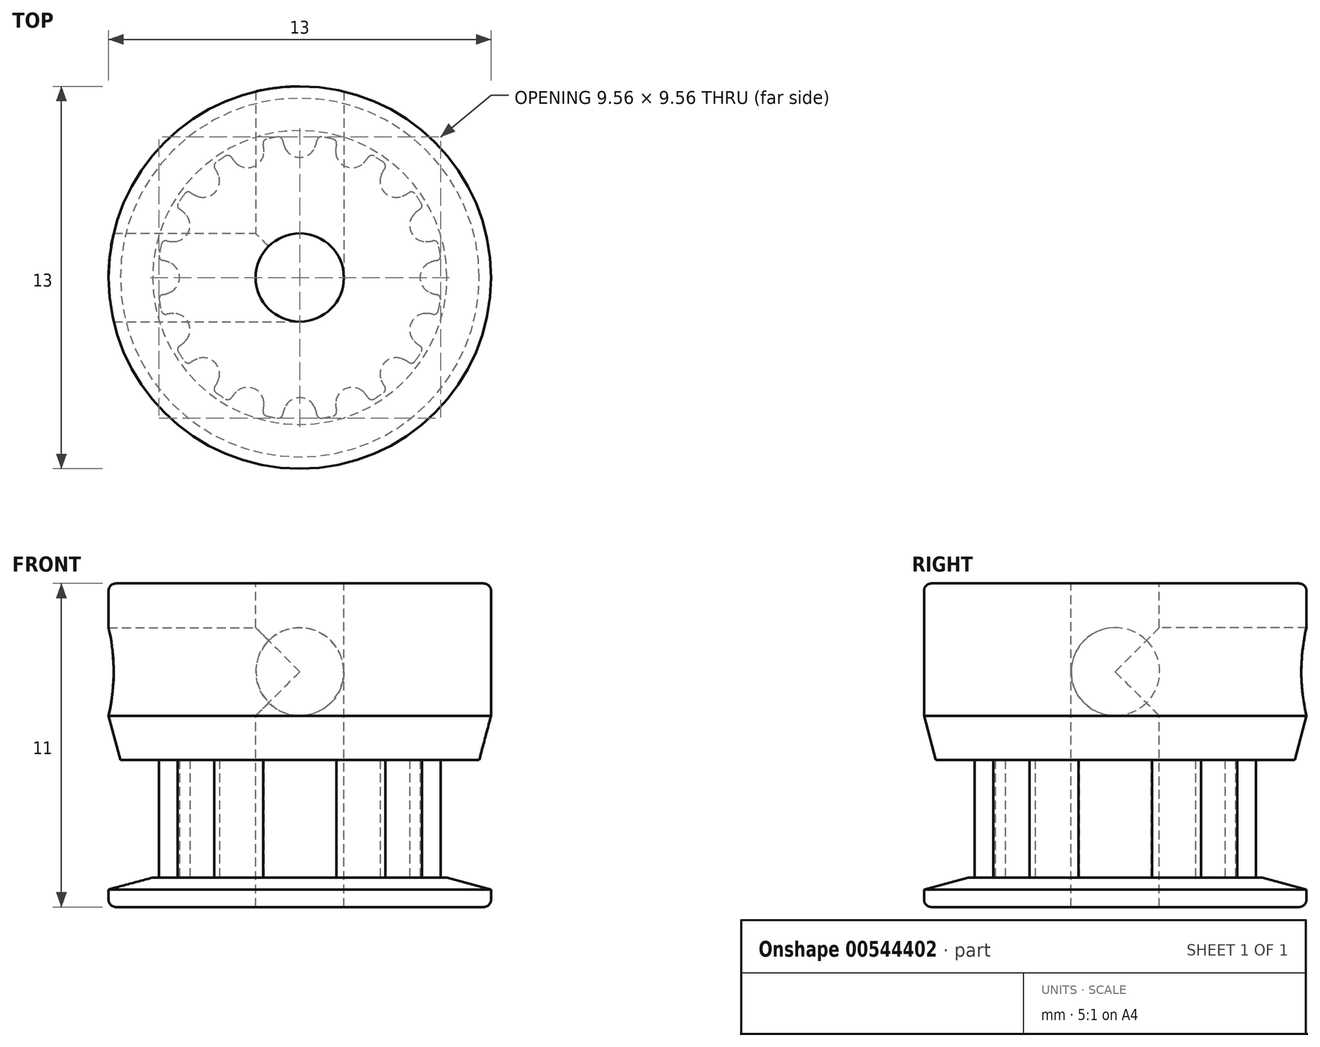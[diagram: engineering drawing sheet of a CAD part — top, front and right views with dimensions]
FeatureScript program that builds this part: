
annotation { "Feature Type Name" : "Feature", "Feature Type Description" : "" }
export const myFeature = defineFeature(function(context is Context, id is Id, definition is map)
    precondition{}
    {
        {
            assignVariable(context, id + "F0", {"name" : "teeth", "anyValue" : 16});
        }
        {
            assignVariable(context, id + "F1", {"name" : "width", "anyValue" : 4});
        }
        {
            var Q0;
            Q0=qCreatedBy(makeId("Top.planeOp"),FACE);
            var sketch = newSketch(context, id + "F2", { "sketchPlane" : qUnion([Q0])});
            skLineSegment(sketch, "E0", {"start": v(0, 0) * mm, "end": v(0, 4.09) * mm, "construction": true});
            skArc(sketch, "E1", {"start": v(1.24, 4.68) * mm, "mid": v(0, 4.84) * mm, "end": v(-1.24, 4.68) * mm, "construction": true});
            skArc(sketch, "E2", {"start": v(0, 4.09) * mm, "mid": v(0.3, 4.18) * mm, "end": v(0.5, 4.42) * mm});
            skLineSegment(sketch, "E3", {"start": v(0, 4.09) * mm, "end": v(0, 4.84) * mm, "construction": true});
            skLineSegment(sketch, "E4", {"start": v(0, 4.84) * mm, "end": v(0, 5.1) * mm, "construction": true});
            skArc(sketch, "E5", {"start": v(1, 5) * mm, "mid": v(0, 5.1) * mm, "end": v(-1, 5) * mm, "construction": true});
            skLineSegment(sketch, "E6", {"start": v(0.94, 4.75) * mm, "end": v(0, 0) * mm});
            skLineSegment(sketch, "E7", {"start": v(0, 0) * mm, "end": v(-0.94, 4.75) * mm});
            skArc(sketch, "E8", {"start": v(0.75, 4.78) * mm, "mid": v(0.64, 4.75) * mm, "end": v(0.58, 4.66) * mm});
            skArc(sketch, "E9", {"start": v(0.5, 4.42) * mm, "mid": v(0.55, 4.53) * mm, "end": v(0.58, 4.66) * mm});
            skArc(sketch, "E10.MirrorCS", {"start": v(0, 4.09) * mm, "mid": v(-0.3, 4.18) * mm, "end": v(-0.5, 4.42) * mm});
            skArc(sketch, "E11.MirrorCS", {"start": v(-0.5, 4.42) * mm, "mid": v(-0.55, 4.53) * mm, "end": v(-0.58, 4.66) * mm});
            skArc(sketch, "E12.MirrorCS", {"start": v(-0.75, 4.78) * mm, "mid": v(-0.64, 4.75) * mm, "end": v(-0.58, 4.66) * mm});
            skArc(sketch, "E13", {"start": v(0, 4.84) * mm, "mid": v(-0.2, 4.83) * mm, "end": v(-0.4, 4.82) * mm, "construction": true});
            skArc(sketch, "E14", {"start": v(1.1, 3.93) * mm, "mid": v(0, 4.09) * mm, "end": v(-1.1, 3.93) * mm, "construction": true});
            skArc(sketch, "E15", {"start": v(-0.75, 4.78) * mm, "mid": v(-0.85, 4.76) * mm, "end": v(-0.94, 4.75) * mm});
            skArc(sketch, "E16", {"start": v(0.75, 4.78) * mm, "mid": v(0.85, 4.76) * mm, "end": v(0.94, 4.75) * mm});
            skPoint(sketch, "E17", {"position": v(0, 4.09) * mm});
            skSolve(sketch);
        }
        {
            var Q0;
            Q0=makeQuery(id+"F2.imprint","IMPRINT",FACE,{"disambiguationData":[TD([[makeQuery(id+"F2.imprint","IMPRINT",EDGE,{"derivedFrom":sQuery(id+"F2.wireOp",EDGE,"E2")}),-1.0]])]});
            var Q1;
            {var subQ1=sQuery(id+"F2.wireOp",EDGE,"N9a9pOVT-NxnP-9PMo-Yz0L-ytRW1WlfzG62");Q1=makeQuery(id+"F2.imprint","IMPRINT",FACE,{"disambiguationData":[TD([[makeQuery(id+"F2.imprint","IMPRINT",EDGE,{"derivedFrom":subQ1}),-1.0]])]});}
            var Q2;
            {var subQ0=sQuery(id+"F2.wireOp",EDGE,"E6");Q2=makeQuery(id+"F2.imprint","IMPRINT",FACE,{"disambiguationData":[TD([[makeQuery(id+"F2.imprint","IMPRINT",EDGE,{"derivedFrom":subQ0}),-1.0]])]});}
            extrude(context, id + "F3", {"entities" : qUnion([Q0, Q1, Q2]), "depth" : (getVariable(context, 'width')) * mm, "offsetDistance" : 25 * mm, "symmetric" : true});
        }
        {
            var Q0;
            Q0=makeQuery(id+"F3.opExtrude","SWEPT_BODY",BODY,{"disambiguationData":[OSD([sQuery(id+"F2.wireOp",EDGE,"E1"),sQuery(id+"F2.wireOp",EDGE,"E2"),sQuery(id+"F2.wireOp",EDGE,"WtW3y5By-gfdo-wMA2-XeKf-OYMCoWhlFWBV"),sQuery(id+"F2.wireOp",EDGE,"E6"),sQuery(id+"F2.wireOp",EDGE,"E7"),sQuery(id+"F2.wireOp",EDGE,"N9a9pOVT-NxnP-9PMo-Yz0L-ytRW1WlfzG62"),sQuery(id+"F2.wireOp",EDGE,"E8"),sQuery(id+"F2.wireOp",EDGE,"E9"),sQuery(id+"F2.wireOp",EDGE,"E10.MirrorCS"),sQuery(id+"F2.wireOp",EDGE,"E11.MirrorCS"),sQuery(id+"F2.wireOp",EDGE,"E12.MirrorCS")])]});
            var Q1;
            Q1=makeQuery(id+"F3.opExtrude","SWEPT_EDGE",EDGE,{"disambiguationData":[OSD([sQuery(id+"F2.wireOp",EDGE,"E6"),sQuery(id+"F2.wireOp",EDGE,"E7")])]});
            circularPattern(context, id + "F4", {"operationType" : NewBodyOperationType.ADD, "entities" : qUnion([Q0]), "axis" : qUnion([Q1]), "angle" : 360 * degree, "instanceCount" : getVariable(context, 'teeth'), "equalSpace" : true});
        }
        {
            var Q0;
            {var subQ0=makeQuery(id+"F3.opExtrude","CAP_FACE",FACE,{"disambiguationData":[OSD([sQuery(id+"F2.wireOp",EDGE,"E2"),sQuery(id+"F2.wireOp",EDGE,"E6"),sQuery(id+"F2.wireOp",EDGE,"E7"),sQuery(id+"F2.wireOp",EDGE,"E8"),sQuery(id+"F2.wireOp",EDGE,"E9"),sQuery(id+"F2.wireOp",EDGE,"E10.MirrorCS"),sQuery(id+"F2.wireOp",EDGE,"E11.MirrorCS"),sQuery(id+"F2.wireOp",EDGE,"E12.MirrorCS"),sQuery(id+"F2.wireOp",EDGE,"E15"),sQuery(id+"F2.wireOp",EDGE,"E16")])],"isStart":true});Q0=makeQuery(id+"F4.boolean.opBoolean","MERGE",FACE,{"derivedFrom":[subQ0,makeQuery(id+"F4.opPattern","COPY",FACE,{"derivedFrom":subQ0,"instanceName":"1"}),makeQuery(id+"F4.opPattern","COPY",FACE,{"derivedFrom":subQ0,"instanceName":"2"}),makeQuery(id+"F4.opPattern","COPY",FACE,{"derivedFrom":subQ0,"instanceName":"3"}),makeQuery(id+"F4.opPattern","COPY",FACE,{"derivedFrom":subQ0,"instanceName":"4"}),makeQuery(id+"F4.opPattern","COPY",FACE,{"derivedFrom":subQ0,"instanceName":"5"}),makeQuery(id+"F4.opPattern","COPY",FACE,{"derivedFrom":subQ0,"instanceName":"6"}),makeQuery(id+"F4.opPattern","COPY",FACE,{"derivedFrom":subQ0,"instanceName":"7"}),makeQuery(id+"F4.opPattern","COPY",FACE,{"derivedFrom":subQ0,"instanceName":"8"}),makeQuery(id+"F4.opPattern","COPY",FACE,{"derivedFrom":subQ0,"instanceName":"9"}),makeQuery(id+"F4.opPattern","COPY",FACE,{"derivedFrom":subQ0,"instanceName":"10"}),makeQuery(id+"F4.opPattern","COPY",FACE,{"derivedFrom":subQ0,"instanceName":"11"}),makeQuery(id+"F4.opPattern","COPY",FACE,{"derivedFrom":subQ0,"instanceName":"12"}),makeQuery(id+"F4.opPattern","COPY",FACE,{"derivedFrom":subQ0,"instanceName":"13"}),makeQuery(id+"F4.opPattern","COPY",FACE,{"derivedFrom":subQ0,"instanceName":"14"}),makeQuery(id+"F4.opPattern","COPY",FACE,{"derivedFrom":subQ0,"instanceName":"15"}),makeQuery(id+"F4.opPattern","COPY",FACE,{"derivedFrom":subQ0,"instanceName":"16"}),makeQuery(id+"F4.opPattern","COPY",FACE,{"derivedFrom":subQ0,"instanceName":"17"}),makeQuery(id+"F4.opPattern","COPY",FACE,{"derivedFrom":subQ0,"instanceName":"18"}),makeQuery(id+"F4.opPattern","COPY",FACE,{"derivedFrom":subQ0,"instanceName":"19"}),makeQuery(id+"F4.opPattern","COPY",FACE,{"derivedFrom":subQ0,"instanceName":"20"}),makeQuery(id+"F4.opPattern","COPY",FACE,{"derivedFrom":subQ0,"instanceName":"21"}),makeQuery(id+"F4.opPattern","COPY",FACE,{"derivedFrom":subQ0,"instanceName":"22"}),makeQuery(id+"F4.opPattern","COPY",FACE,{"derivedFrom":subQ0,"instanceName":"23"}),makeQuery(id+"F4.opPattern","COPY",FACE,{"derivedFrom":subQ0,"instanceName":"24"}),makeQuery(id+"F4.opPattern","COPY",FACE,{"derivedFrom":subQ0,"instanceName":"25"}),makeQuery(id+"F4.opPattern","COPY",FACE,{"derivedFrom":subQ0,"instanceName":"26"}),makeQuery(id+"F4.opPattern","COPY",FACE,{"derivedFrom":subQ0,"instanceName":"27"}),makeQuery(id+"F4.opPattern","COPY",FACE,{"derivedFrom":subQ0,"instanceName":"28"}),makeQuery(id+"F4.opPattern","COPY",FACE,{"derivedFrom":subQ0,"instanceName":"29"}),makeQuery(id+"F4.opPattern","COPY",FACE,{"derivedFrom":subQ0,"instanceName":"30"}),makeQuery(id+"F4.opPattern","COPY",FACE,{"derivedFrom":subQ0,"instanceName":"31"}),makeQuery(id+"F4.opPattern","COPY",FACE,{"derivedFrom":subQ0,"instanceName":"32"}),makeQuery(id+"F4.opPattern","COPY",FACE,{"derivedFrom":subQ0,"instanceName":"33"}),makeQuery(id+"F4.opPattern","COPY",FACE,{"derivedFrom":subQ0,"instanceName":"34"}),makeQuery(id+"F4.opPattern","COPY",FACE,{"derivedFrom":subQ0,"instanceName":"35"}),makeQuery(id+"F4.opPattern","COPY",FACE,{"derivedFrom":subQ0,"instanceName":"36"}),makeQuery(id+"F4.opPattern","COPY",FACE,{"derivedFrom":subQ0,"instanceName":"37"}),makeQuery(id+"F4.opPattern","COPY",FACE,{"derivedFrom":subQ0,"instanceName":"38"}),makeQuery(id+"F4.opPattern","COPY",FACE,{"derivedFrom":subQ0,"instanceName":"39"})]});}
            var sketch = newSketch(context, id + "F5", { "sketchPlane" : qUnion([Q0])});
            skCircle(sketch, "E18", {"center": v(0, 0) * mm, "radius": 6.5 * mm});
            skSolve(sketch);
        }
        {
            var Q0;
            Q0=qSketchRegion(id+"F5",true);
            extrude(context, id + "F6", {"entities" : qUnion([Q0]), "operationType" : NewBodyOperationType.ADD, "depth" : 1 * mm, "offsetDistance" : 25 * mm});
        }
        {
            var Q0;
            {var subQ0=makeQuery(id+"F3.opExtrude","CAP_FACE",FACE,{"disambiguationData":[OSD([sQuery(id+"F2.wireOp",EDGE,"E2"),sQuery(id+"F2.wireOp",EDGE,"E6"),sQuery(id+"F2.wireOp",EDGE,"E7"),sQuery(id+"F2.wireOp",EDGE,"E8"),sQuery(id+"F2.wireOp",EDGE,"E9"),sQuery(id+"F2.wireOp",EDGE,"E10.MirrorCS"),sQuery(id+"F2.wireOp",EDGE,"E11.MirrorCS"),sQuery(id+"F2.wireOp",EDGE,"E12.MirrorCS"),sQuery(id+"F2.wireOp",EDGE,"E15"),sQuery(id+"F2.wireOp",EDGE,"E16")])],"isStart":false});Q0=makeQuery(id+"F4.boolean.opBoolean","MERGE",FACE,{"derivedFrom":[subQ0,makeQuery(id+"F4.opPattern","COPY",FACE,{"derivedFrom":subQ0,"instanceName":"1"}),makeQuery(id+"F4.opPattern","COPY",FACE,{"derivedFrom":subQ0,"instanceName":"2"}),makeQuery(id+"F4.opPattern","COPY",FACE,{"derivedFrom":subQ0,"instanceName":"3"}),makeQuery(id+"F4.opPattern","COPY",FACE,{"derivedFrom":subQ0,"instanceName":"4"}),makeQuery(id+"F4.opPattern","COPY",FACE,{"derivedFrom":subQ0,"instanceName":"5"}),makeQuery(id+"F4.opPattern","COPY",FACE,{"derivedFrom":subQ0,"instanceName":"6"}),makeQuery(id+"F4.opPattern","COPY",FACE,{"derivedFrom":subQ0,"instanceName":"7"}),makeQuery(id+"F4.opPattern","COPY",FACE,{"derivedFrom":subQ0,"instanceName":"8"}),makeQuery(id+"F4.opPattern","COPY",FACE,{"derivedFrom":subQ0,"instanceName":"9"}),makeQuery(id+"F4.opPattern","COPY",FACE,{"derivedFrom":subQ0,"instanceName":"10"}),makeQuery(id+"F4.opPattern","COPY",FACE,{"derivedFrom":subQ0,"instanceName":"11"}),makeQuery(id+"F4.opPattern","COPY",FACE,{"derivedFrom":subQ0,"instanceName":"12"}),makeQuery(id+"F4.opPattern","COPY",FACE,{"derivedFrom":subQ0,"instanceName":"13"}),makeQuery(id+"F4.opPattern","COPY",FACE,{"derivedFrom":subQ0,"instanceName":"14"}),makeQuery(id+"F4.opPattern","COPY",FACE,{"derivedFrom":subQ0,"instanceName":"15"}),makeQuery(id+"F4.opPattern","COPY",FACE,{"derivedFrom":subQ0,"instanceName":"16"}),makeQuery(id+"F4.opPattern","COPY",FACE,{"derivedFrom":subQ0,"instanceName":"17"}),makeQuery(id+"F4.opPattern","COPY",FACE,{"derivedFrom":subQ0,"instanceName":"18"}),makeQuery(id+"F4.opPattern","COPY",FACE,{"derivedFrom":subQ0,"instanceName":"19"}),makeQuery(id+"F4.opPattern","COPY",FACE,{"derivedFrom":subQ0,"instanceName":"20"}),makeQuery(id+"F4.opPattern","COPY",FACE,{"derivedFrom":subQ0,"instanceName":"21"}),makeQuery(id+"F4.opPattern","COPY",FACE,{"derivedFrom":subQ0,"instanceName":"22"}),makeQuery(id+"F4.opPattern","COPY",FACE,{"derivedFrom":subQ0,"instanceName":"23"}),makeQuery(id+"F4.opPattern","COPY",FACE,{"derivedFrom":subQ0,"instanceName":"24"}),makeQuery(id+"F4.opPattern","COPY",FACE,{"derivedFrom":subQ0,"instanceName":"25"}),makeQuery(id+"F4.opPattern","COPY",FACE,{"derivedFrom":subQ0,"instanceName":"26"}),makeQuery(id+"F4.opPattern","COPY",FACE,{"derivedFrom":subQ0,"instanceName":"27"}),makeQuery(id+"F4.opPattern","COPY",FACE,{"derivedFrom":subQ0,"instanceName":"28"}),makeQuery(id+"F4.opPattern","COPY",FACE,{"derivedFrom":subQ0,"instanceName":"29"}),makeQuery(id+"F4.opPattern","COPY",FACE,{"derivedFrom":subQ0,"instanceName":"30"}),makeQuery(id+"F4.opPattern","COPY",FACE,{"derivedFrom":subQ0,"instanceName":"31"}),makeQuery(id+"F4.opPattern","COPY",FACE,{"derivedFrom":subQ0,"instanceName":"32"}),makeQuery(id+"F4.opPattern","COPY",FACE,{"derivedFrom":subQ0,"instanceName":"33"}),makeQuery(id+"F4.opPattern","COPY",FACE,{"derivedFrom":subQ0,"instanceName":"34"}),makeQuery(id+"F4.opPattern","COPY",FACE,{"derivedFrom":subQ0,"instanceName":"35"}),makeQuery(id+"F4.opPattern","COPY",FACE,{"derivedFrom":subQ0,"instanceName":"36"}),makeQuery(id+"F4.opPattern","COPY",FACE,{"derivedFrom":subQ0,"instanceName":"37"}),makeQuery(id+"F4.opPattern","COPY",FACE,{"derivedFrom":subQ0,"instanceName":"38"}),makeQuery(id+"F4.opPattern","COPY",FACE,{"derivedFrom":subQ0,"instanceName":"39"})]});}
            var sketch = newSketch(context, id + "F7", { "sketchPlane" : qUnion([Q0])});
            skCircle(sketch, "E19", {"center": v(0, 0) * mm, "radius": 6.5 * mm});
            skSolve(sketch);
        }
        {
            var Q0;
            Q0=qSketchRegion(id+"F7",true);
            extrude(context, id + "F8", {"entities" : qUnion([Q0]), "operationType" : NewBodyOperationType.ADD, "depth" : 1 * mm, "offsetDistance" : 25 * mm});
        }
        {
            var Q0;
            Q0=makeQuery(id+"F8.opExtrude","CAP_FACE",FACE,{"disambiguationData":[OSD([sQuery(id+"F7.wireOp",EDGE,"E19")])],"isStart":false});
            var sketch = newSketch(context, id + "F9", { "sketchPlane" : qUnion([Q0])});
            skCircle(sketch, "E20", {"center": v(0, 0) * mm, "radius": 6.5 * mm});
            skSolve(sketch);
        }
        {
            var Q0;
            Q0=qSketchRegion(id+"F9",true);
            extrude(context, id + "F10", {"entities" : qUnion([Q0]), "operationType" : NewBodyOperationType.ADD, "depth" : (6 - 1) * mm, "offsetDistance" : 25 * mm});
        }
        {
            var Q0;
            Q0=makeQuery(id+"F10.opExtrude","CAP_FACE",FACE,{"disambiguationData":[OSD([sQuery(id+"F9.wireOp",EDGE,"E20")])],"isStart":false});
            var sketch = newSketch(context, id + "F11", { "sketchPlane" : qUnion([Q0])});
            skCircle(sketch, "E21", {"center": v(0, 0) * mm, "radius": 1.5 * mm});
            skSolve(sketch);
        }
        {
            var Q0;
            Q0=qSketchRegion(id+"F11",true);
            extrude(context, id + "F12", {"entities" : qUnion([Q0]), "operationType" : NewBodyOperationType.REMOVE, "endBound" : BoundingType.THROUGH_ALL, "oppositeDirection" : true, "depth" : 25 * mm, "offsetDistance" : 25 * mm});
        }
        {
            var Q0;
            Q0=qCreatedBy(makeId("Front.planeOp"),FACE);
            var sketch = newSketch(context, id + "F13", { "sketchPlane" : qUnion([Q0])});
            skCircle(sketch, "E22", {"center": v(0, 5) * mm, "radius": 1.5 * mm});
            skLineSegment(sketch, "E23", {"start": v(8.86, 5) * mm, "end": v(-9.17, 5) * mm, "construction": true});
            skSolve(sketch);
        }
        {
            var Q0;
            Q0=qSketchRegion(id+"F13",true);
            extrude(context, id + "F14", {"entities" : qUnion([Q0]), "operationType" : NewBodyOperationType.REMOVE, "endBound" : BoundingType.THROUGH_ALL, "oppositeDirection" : true, "depth" : 25 * mm, "offsetDistance" : 25 * mm});
        }
        {
            var Q0;
            Q0=qCreatedBy(makeId("Right.planeOp"),FACE);
            var sketch = newSketch(context, id + "F15", { "sketchPlane" : qUnion([Q0])});
            skCircle(sketch, "E24", {"center": v(0, 5) * mm, "radius": 1.5 * mm});
            skLineSegment(sketch, "E25", {"start": v(-7.7, 5) * mm, "end": v(8.04, 5) * mm, "construction": true});
            skSolve(sketch);
        }
        {
            var Q0;
            Q0=qSketchRegion(id+"F15",true);
            extrude(context, id + "F16", {"entities" : qUnion([Q0]), "operationType" : NewBodyOperationType.REMOVE, "endBound" : BoundingType.THROUGH_ALL, "oppositeDirection" : true, "depth" : 25 * mm, "offsetDistance" : 25 * mm});
        }
        {
            var Q0;
            Q0=makeQuery(id+"F6.opExtrude","CAP_EDGE",EDGE,{"disambiguationData":[OSD([sQuery(id+"F5.wireOp",EDGE,"E18")])],"isStart":true});
            var Q1;
            Q1=makeQuery(id+"F8.opExtrude","CAP_EDGE",EDGE,{"disambiguationData":[OSD([sQuery(id+"F7.wireOp",EDGE,"E19")])],"isStart":true});
            chamfer(context, id + "F17", {"entities" : qUnion([Q0, Q1]), "chamferType" : ChamferType.OFFSET_ANGLE, "width" : 1.5 * mm, "oppositeDirection" : true, "angle" : 15 * degree, "tangentPropagation" : true});
        }
        {
            var Q0;
            Q0=makeQuery(id+"F10.opExtrude","CAP_EDGE",EDGE,{"disambiguationData":[OSD([sQuery(id+"F9.wireOp",EDGE,"E20")])],"isStart":true});
            var Q1;
            Q1=makeQuery(id+"F10.opExtrude","CAP_EDGE",EDGE,{"disambiguationData":[OSD([sQuery(id+"F9.wireOp",EDGE,"E20")])],"isStart":false});
            var Q2;
            Q2=makeQuery(id+"F8.opExtrude","CAP_EDGE",EDGE,{"disambiguationData":[OSD([sQuery(id+"F7.wireOp",EDGE,"E19")])],"isStart":false});
            var Q3;
            Q3=makeQuery(id+"F6.opExtrude","CAP_EDGE",EDGE,{"disambiguationData":[OSD([sQuery(id+"F5.wireOp",EDGE,"E18")])],"isStart":false});
            fillet(context, id + "F18", {"entities" : qUnion([Q0, Q1, Q2, Q3]), "radius" : 0.25 * mm, "tangentPropagation" : true, "allowEdgeOverflow" : false});
        }
    });
